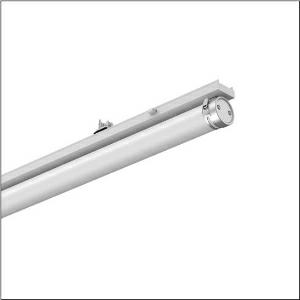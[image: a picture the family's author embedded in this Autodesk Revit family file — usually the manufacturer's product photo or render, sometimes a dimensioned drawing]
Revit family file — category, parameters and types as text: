
# Revit family: monsun_31_tube_51ft10nn4a0atr1
name_source: partatom
category: Lighting Fixtures
units: mm (PartAtom-declared; Revit-internal decimal feet)

## family parameters
Cut with Voids When Loaded = No
Host = Face
Light Source = No
Part Type = Normal
Room Calculation Point = No
Round Connector Dimension = Use Diameter
Shared = No

## types (1)
- --- (1 x LED, 10000 lm, 58 W, 4000K)
    Apparent Load = 58 VA
    CIE Flux Codes = 42 71 90 91 100
    Color Rendering = 80
    Color Temperature = 4000K
    Default Elevation = 1800 mm
    Description = Monsun 31 Tube, tubular luminaire, primary optical cover: diffuser, of PMMA, light emission: direct distribution, primary light characteristic: symmetric, LED, rated luminous flux: 10.000lm, luminous efficacy: 172lm/W, light colour: 840, colour temperature: 4000K, control gear: DALI Multilumen, with with 1 terminal, 5-pole, max. 2.5mm², mains connection: 220..240V, AC, 50/60Hz, rated input power: 58W, housing, cylindrical, of PMMA, semi-transparent, matt white, with luminaire and ceiling fastening, V4A, mounting with brackets of stainless steel, length: 1.495mm, diameter: 75mm, end cap, of stainless steel (V4A), protection rating (complete): IP20, protection rating (lamp compartment): IP67/69K, insulation class (complete): insulation class I (protective earthing), certification: CE, UKCA, impact resistance: IK07, permissible operating ambient temperature: -20..+40°C, corresponds to IFS (International Featured Standards) requirements for safety and quality in the food industry, contact your sales advisor before using the luminaires in applications with unclear chemical exposure, large temperature fluctuations or condensation-forming humidity, packaging unit: 1 piece
    Height = 118 mm
    Lamp = 1 x LED
    Lamp Light Flux = 10000 lm
    Lamp Power = 58 W
    Lamp count = 1
    Length = 1495 mm
    Luminous efficacy = 172 lm/W
    Manufacturer = Siteco
    ModVariant = No
    Model = 51FT10NN4A0ATR1
    Mounting Place = Ceiling
    Mounting Type = Pendant
    Number of Poles = 1
    OnlyDefault = Yes
    Power Factor = 1
    Product Name = Monsun 31 Tube
    Product group = tubular luminaire
    ProductGroupID = 906
    Protection Class = Protection class I
    Protection Degree = IP 20
    RLX_Detail_Level = 1
    RLX_Emergency_Light_Flux = 0 lm
    RLX_Emergency_Type = 0
    RLX_Emergency_Type_DB = No
    RlxData = <blob elided: 32273 chars, md5=3563155c>
    Socket = socket
    Standby Power = 0 W
    System Light Flux = 10000 lm
    System Power = 58 W
    Type Comments = individual setting: luminous flux: 100 % | (OFF | OFF | ON | OFF) | 350 mA
    Type Image = l_1007227.jpg
    URL = http://relux.com
    VarID = @adj_142865
    Voltage = 0 V
    Weight = 0.00 kg
    Width = 75 mm

## geometry (parser evidence)
native form markers: Blend x4, Sweep x10
no freeform markers — native parametric forms only
